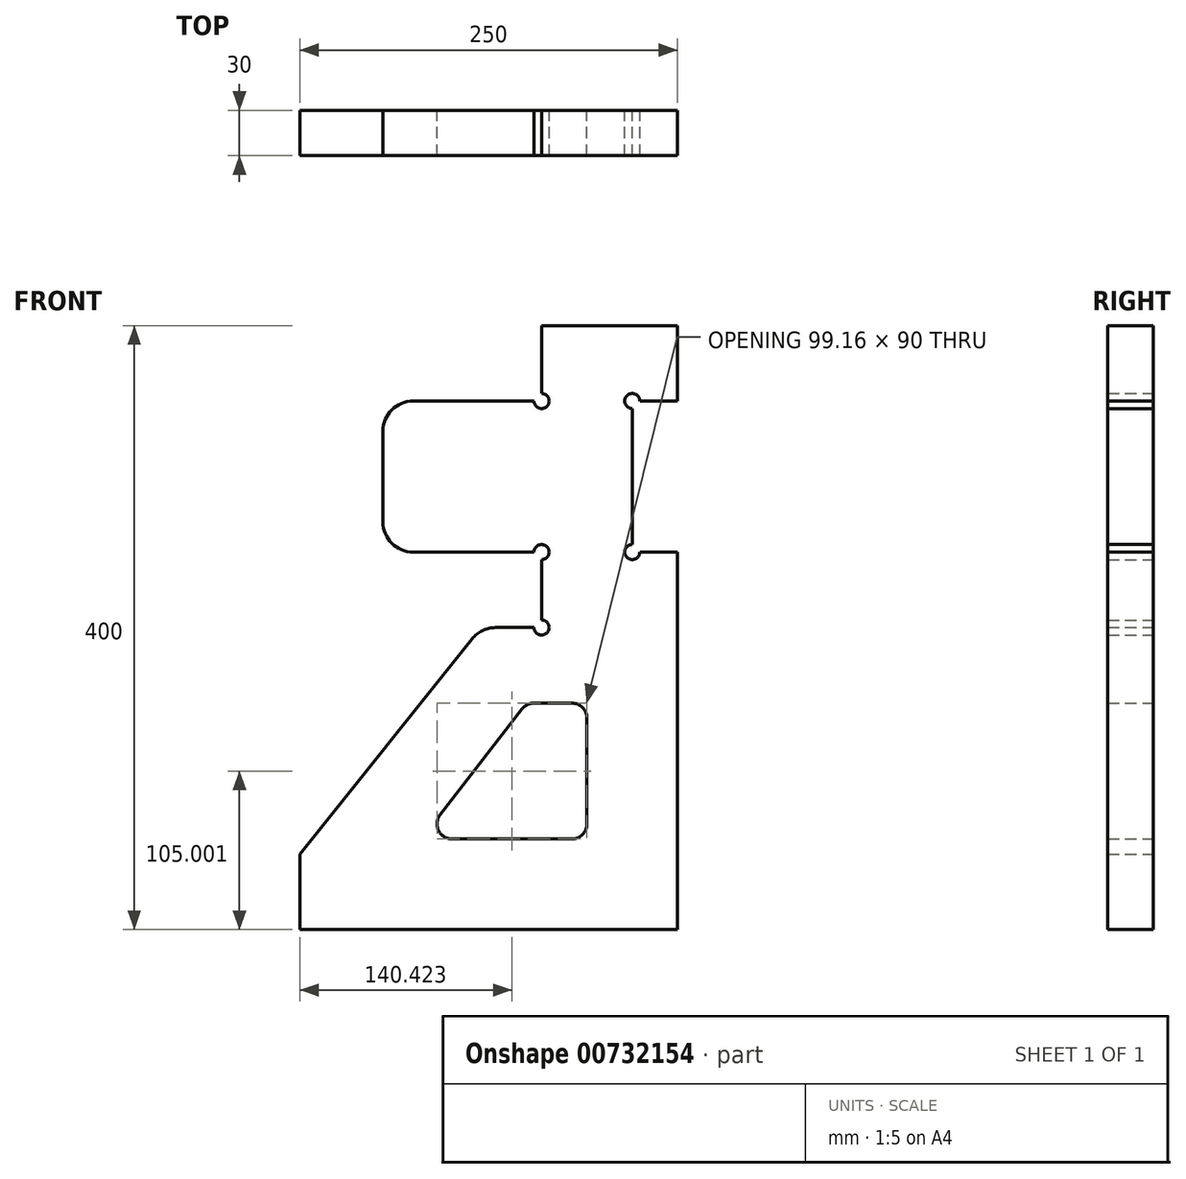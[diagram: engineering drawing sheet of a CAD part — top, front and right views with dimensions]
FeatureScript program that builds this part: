
annotation { "Feature Type Name" : "Feature", "Feature Type Description" : "" }
export const myFeature = defineFeature(function(context is Context, id is Id, definition is map)
    precondition{}
    {
        {
            var Q0;
            Q0=qCreatedBy(makeId("Front.planeOp"),FACE);
            var sketch = newSketch(context, id + "F0", { "sketchPlane" : qUnion([Q0])});
            skLineSegment(sketch, "E0.bottom", {"start": v(47.2, 120.78) * mm, "end": v(297.2, 120.78) * mm});
            skLineSegment(sketch, "E0.top", {"start": v(207.2, 520.78) * mm, "end": v(297.2, 520.78) * mm});
            skLineSegment(sketch, "E0.left", {"start": v(47.2, 120.78) * mm, "end": v(47.2, 170.78) * mm});
            skLineSegment(sketch, "E1.bottom", {"start": v(297.2, 520.78) * mm, "end": v(207.2, 520.78) * mm});
            skLineSegment(sketch, "E2.bottom", {"start": v(202.2, 470.78) * mm, "end": v(122.2, 470.78) * mm});
            skLineSegment(sketch, "E2.top", {"start": v(202.2, 370.78) * mm, "end": v(122.2, 370.78) * mm});
            skLineSegment(sketch, "E2.right", {"start": v(102.2, 450.78) * mm, "end": v(102.2, 390.78) * mm});
            skLineSegment(sketch, "E3", {"start": v(202.2, 320.78) * mm, "end": v(176.8, 320.78) * mm});
            skLineSegment(sketch, "E4", {"start": v(207.2, 475.78) * mm, "end": v(207.2, 520.78) * mm});
            skLineSegment(sketch, "E5", {"start": v(207.2, 365.78) * mm, "end": v(207.2, 325.78) * mm});
            skArc(sketch, "E6", {"start": v(202.2, 470.78) * mm, "mid": v(210.73, 467.25) * mm, "end": v(207.2, 475.78) * mm});
            skArc(sketch, "E7", {"start": v(207.2, 365.78) * mm, "mid": v(210.73, 374.32) * mm, "end": v(202.2, 370.78) * mm});
            skLineSegment(sketch, "E8", {"start": v(47.2, 170.78) * mm, "end": v(161.19, 313.28) * mm});
            skPoint(sketch, "E9.visualSharp", {"position": v(102.2, 470.78) * mm});
            skArc(sketch, "E9.filletArc", {"start": v(122.2, 470.78) * mm, "mid": v(108.05, 464.92) * mm, "end": v(102.2, 450.78) * mm});
            skPoint(sketch, "E10.visualSharp", {"position": v(102.2, 370.78) * mm});
            skArc(sketch, "E10.filletArc", {"start": v(102.2, 390.78) * mm, "mid": v(108.05, 376.64) * mm, "end": v(122.2, 370.78) * mm});
            skPoint(sketch, "E11.visualSharp", {"position": v(167.2, 320.78) * mm});
            skArc(sketch, "E11.filletArc", {"start": v(176.8, 320.78) * mm, "mid": v(168.14, 318.8) * mm, "end": v(161.19, 313.28) * mm});
            skLineSegment(sketch, "E12", {"start": v(297.2, 120.78) * mm, "end": v(297.2, 370.78) * mm});
            skPoint(sketch, "E13.visualSharp", {"position": v(87.2, 170.78) * mm});
            skPoint(sketch, "E14.visualSharp", {"position": v(207.2, 320.78) * mm});
            skLineSegment(sketch, "E15", {"start": v(147.98, 170.78) * mm, "end": v(227.2, 170.78) * mm});
            skLineSegment(sketch, "E16", {"start": v(247.2, 190.78) * mm, "end": v(247.2, 260.78) * mm});
            skLineSegment(sketch, "E17", {"start": v(227.2, 280.78) * mm, "end": v(202.2, 280.78) * mm});
            skLineSegment(sketch, "E18", {"start": v(132.17, 203.03) * mm, "end": v(186.38, 273.03) * mm});
            skPoint(sketch, "E19.visualSharp", {"position": v(107.2, 170.78) * mm});
            skArc(sketch, "E19.filletArc", {"start": v(132.17, 203.03) * mm, "mid": v(130.02, 181.98) * mm, "end": v(147.98, 170.78) * mm});
            skPoint(sketch, "E20.visualSharp", {"position": v(192.39, 280.78) * mm});
            skArc(sketch, "E20.filletArc", {"start": v(202.2, 280.78) * mm, "mid": v(193.39, 278.74) * mm, "end": v(186.38, 273.03) * mm});
            skPoint(sketch, "E21.visualSharp", {"position": v(247.2, 280.78) * mm});
            skArc(sketch, "E21.filletArc", {"start": v(247.2, 260.78) * mm, "mid": v(241.34, 274.92) * mm, "end": v(227.2, 280.78) * mm});
            skPoint(sketch, "E22.visualSharp", {"position": v(247.2, 170.78) * mm});
            skArc(sketch, "E22.filletArc", {"start": v(227.2, 170.78) * mm, "mid": v(241.34, 176.64) * mm, "end": v(247.2, 190.78) * mm});
            skArc(sketch, "E23", {"start": v(202.2, 320.78) * mm, "mid": v(210.73, 317.25) * mm, "end": v(207.2, 325.78) * mm});
            skLineSegment(sketch, "E24.bottom", {"start": v(297.2, 470.78) * mm, "end": v(272.2, 470.78) * mm});
            skLineSegment(sketch, "E24.top", {"start": v(297.2, 370.78) * mm, "end": v(272.2, 370.78) * mm});
            skLineSegment(sketch, "E24.right", {"start": v(267.2, 465.78) * mm, "end": v(267.2, 375.78) * mm});
            skLineSegment(sketch, "E25.trimOffspring", {"start": v(297.2, 470.78) * mm, "end": v(297.2, 520.78) * mm});
            skArc(sketch, "E26", {"start": v(272.2, 470.78) * mm, "mid": v(263.66, 474.32) * mm, "end": v(267.2, 465.78) * mm});
            skArc(sketch, "E27", {"start": v(267.2, 375.78) * mm, "mid": v(263.66, 367.25) * mm, "end": v(272.2, 370.78) * mm});
            skArc(sketch, "E28.0", {"start": v(140.07, 196.9) * mm, "mid": v(139, 186.38) * mm, "end": v(147.98, 180.78) * mm});
            skLineSegment(sketch, "E28.1", {"start": v(147.98, 180.78) * mm, "end": v(227.2, 180.78) * mm});
            skLineSegment(sketch, "E28.2", {"start": v(140.07, 196.9) * mm, "end": v(194.29, 266.9) * mm});
            skArc(sketch, "E28.3", {"start": v(227.2, 180.78) * mm, "mid": v(234.26, 183.71) * mm, "end": v(237.2, 190.78) * mm});
            skArc(sketch, "E28.4", {"start": v(202.2, 270.78) * mm, "mid": v(197.8, 269.76) * mm, "end": v(194.29, 266.9) * mm});
            skLineSegment(sketch, "E28.5", {"start": v(227.2, 270.78) * mm, "end": v(202.2, 270.78) * mm});
            skArc(sketch, "E28.6", {"start": v(237.2, 260.78) * mm, "mid": v(234.26, 267.85) * mm, "end": v(227.2, 270.78) * mm});
            skLineSegment(sketch, "E28.7", {"start": v(237.2, 190.78) * mm, "end": v(237.2, 260.78) * mm});
            skSolve(sketch);
        }
        {
            var Q0;
            Q0 = qSketchRegion(id + "F0", true);
            var Q1;
            Q1=makeQuery(id+"F0.imprint","IMPRINT",FACE,{"disambiguationData":[TD([[makeQuery(id+"F0.imprint","IMPRINT",EDGE,{"derivedFrom":sQuery(id+"F0.wireOp",EDGE,"E15")}),1.0]])]});
            extrude(context, id + "F1", {"entities" : qUnion([Q0, Q1]), "depth" : 30 * mm, "offsetDistance" : 25 * mm});
        }
    });
